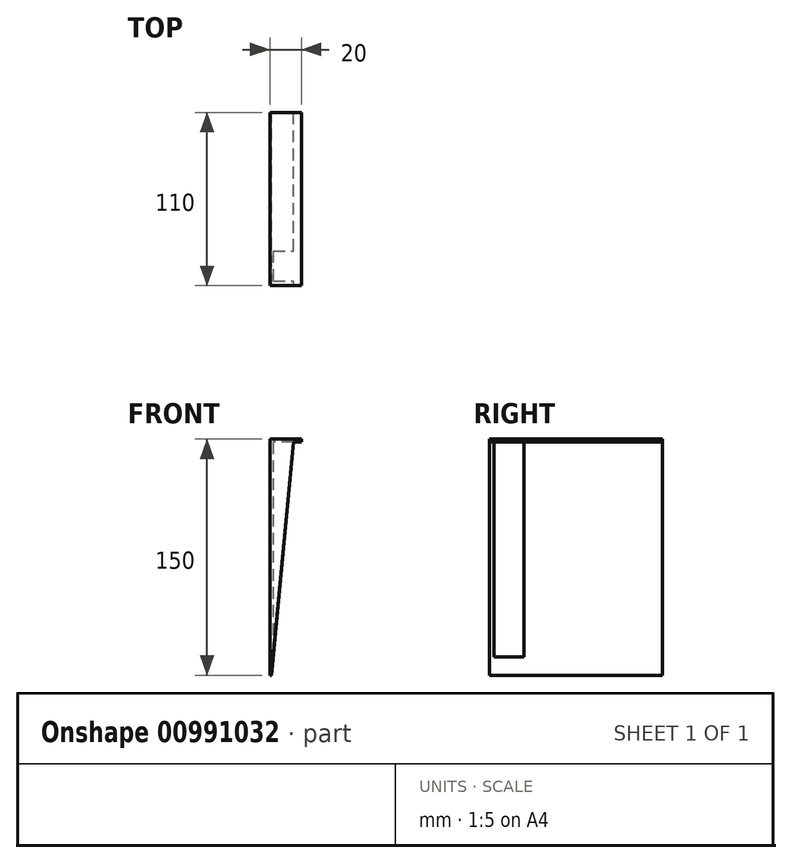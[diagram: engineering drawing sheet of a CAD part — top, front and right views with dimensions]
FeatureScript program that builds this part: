
annotation { "Feature Type Name" : "Feature", "Feature Type Description" : "" }
export const myFeature = defineFeature(function(context is Context, id is Id, definition is map)
    precondition{}
    {
        {
            var Q0;
            Q0=qCreatedBy(makeId("Front.planeOp"),FACE);
            var sketch = newSketch(context, id + "F0", { "sketchPlane" : qUnion([Q0])});
            skLineSegment(sketch, "E0", {"start": v(0, 17.6) * mm, "end": v(20, 17.6) * mm});
            skLineSegment(sketch, "E1", {"start": v(20, 17.6) * mm, "end": v(20, 15.6) * mm});
            skLineSegment(sketch, "E2", {"start": v(20, 15.6) * mm, "end": v(15, 15.6) * mm});
            skLineSegment(sketch, "E3", {"start": v(15, 15.6) * mm, "end": v(0.9, -132.4) * mm});
            skLineSegment(sketch, "E4", {"start": v(0.9, -132.4) * mm, "end": v(0, -132.4) * mm});
            skLineSegment(sketch, "E5", {"start": v(0, -132.4) * mm, "end": v(0, 17.6) * mm});
            skSolve(sketch);
        }
        {
            var Q0;
            Q0 = qSketchRegion(id + "F0", true);
            extrude(context, id + "F1", {"entities" : qUnion([Q0]), "depth" : 110 * mm, "offsetDistance" : 25 * mm});
        }
        {
            var Q0;
            Q0=qCreatedBy(makeId("Right.planeOp"),FACE);
            cPlane(context, id + "F2", {"entities" : qUnion([Q0]), "cplaneType" : CPlaneType.OFFSET, "offset" : 2 * mm, "width" : 150 * mm, "height" : 150 * mm});
        }
        {
            var Q0;
            Q0=qCreatedBy(id+"F2.planeOp",FACE);
            var sketch = newSketch(context, id + "F3", { "sketchPlane" : qUnion([Q0])});
            skLineSegment(sketch, "E6.bottom", {"start": v(-107, 15.6) * mm, "end": v(-88, 15.6) * mm});
            skLineSegment(sketch, "E6.top", {"start": v(-107, -132.4) * mm, "end": v(-88, -132.4) * mm});
            skLineSegment(sketch, "E6.left", {"start": v(-107, 15.6) * mm, "end": v(-107, -132.4) * mm});
            skLineSegment(sketch, "E6.right", {"start": v(-88, 15.6) * mm, "end": v(-88, -132.4) * mm});
            skSolve(sketch);
        }
        {
            var Q0;
            Q0 = qSketchRegion(id + "F3", true);
            extrude(context, id + "F4", {"entities" : qUnion([Q0]), "operationType" : NewBodyOperationType.REMOVE, "endBound" : BoundingType.THROUGH_ALL, "depth" : 25 * mm, "offsetDistance" : 25 * mm});
        }
    });
